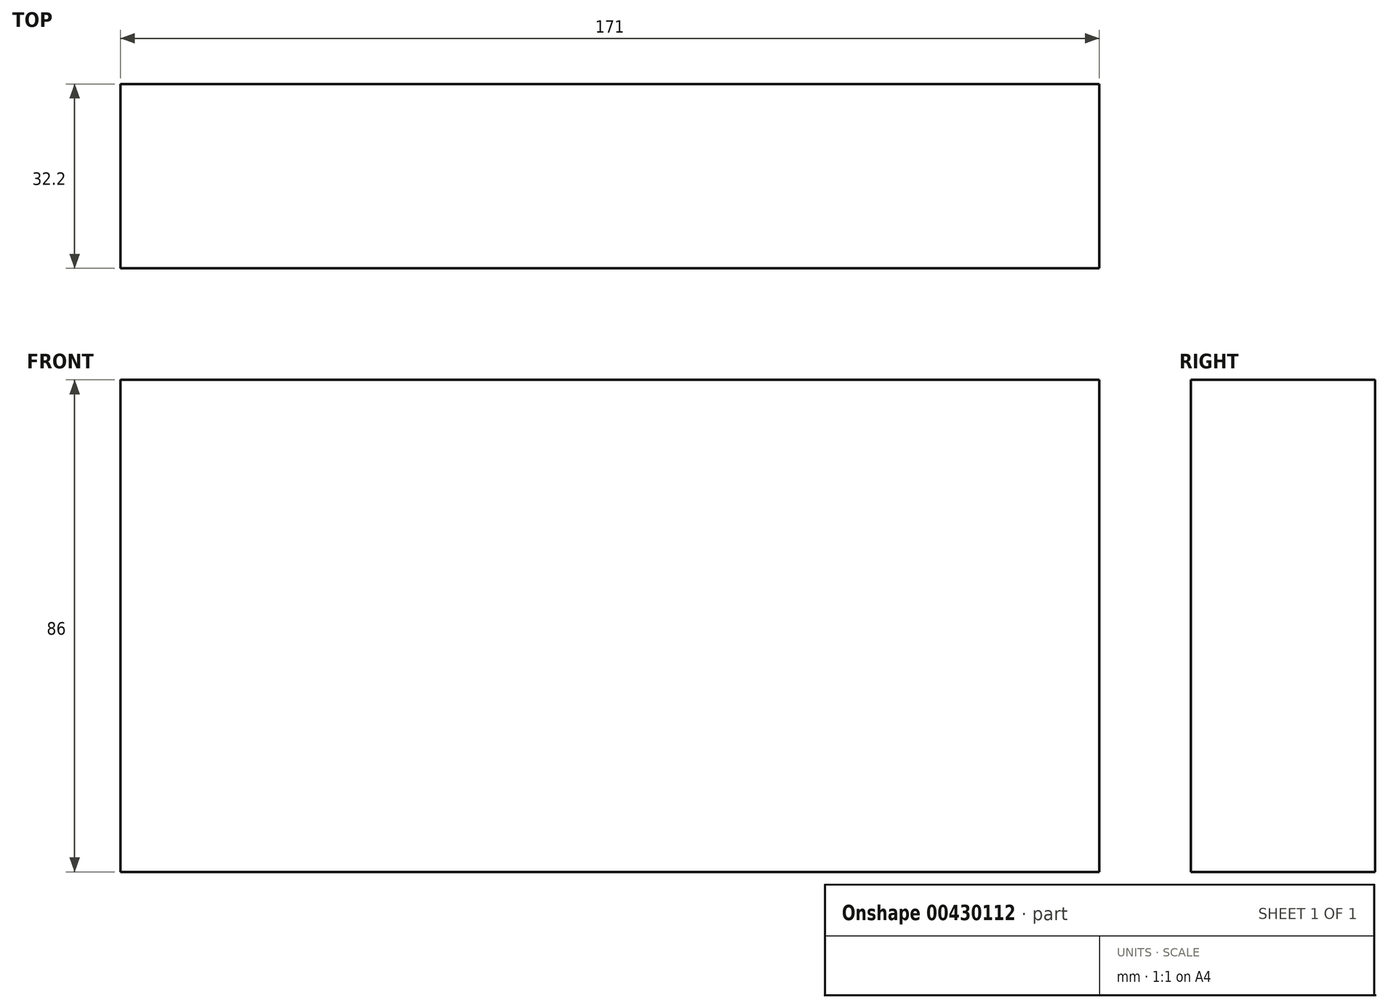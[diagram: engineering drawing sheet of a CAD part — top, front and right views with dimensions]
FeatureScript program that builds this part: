
annotation { "Feature Type Name" : "Feature", "Feature Type Description" : "" }
export const myFeature = defineFeature(function(context is Context, id is Id, definition is map)
    precondition{}
    {
        {
            var Q0;
            Q0=qCreatedBy(makeId("Front.planeOp"),FACE);
            var sketch = newSketch(context, id + "F0", { "sketchPlane" : qUnion([Q0])});
            skLineSegment(sketch, "E0.bottom", {"start": v(0, 0) * mm, "end": v(-171, 0) * mm});
            skLineSegment(sketch, "E0.top", {"start": v(0, 86) * mm, "end": v(-171, 86) * mm});
            skLineSegment(sketch, "E0.right", {"start": v(-171, 0) * mm, "end": v(-171, 86) * mm});
            skLineSegment(sketch, "E1.trimOffspring", {"start": v(0, 0) * mm, "end": v(0, 86) * mm});
            skPoint(sketch, "E2.left.start.orphan", {"position": v(0, 3.1) * mm});
            skSolve(sketch);
        }
        {
            var Q0;
            Q0=makeQuery(id+"F0.imprint","IMPRINT",FACE,{"disambiguationData":[TD([[makeQuery(id+"F0.imprint","IMPRINT",EDGE,{"derivedFrom":sQuery(id+"F0.wireOp",EDGE,"E0.bottom")}),-1.0]])]});
            extrude(context, id + "F1", {"entities" : qUnion([Q0]), "depth" : 32.2 * mm});
        }
    });
